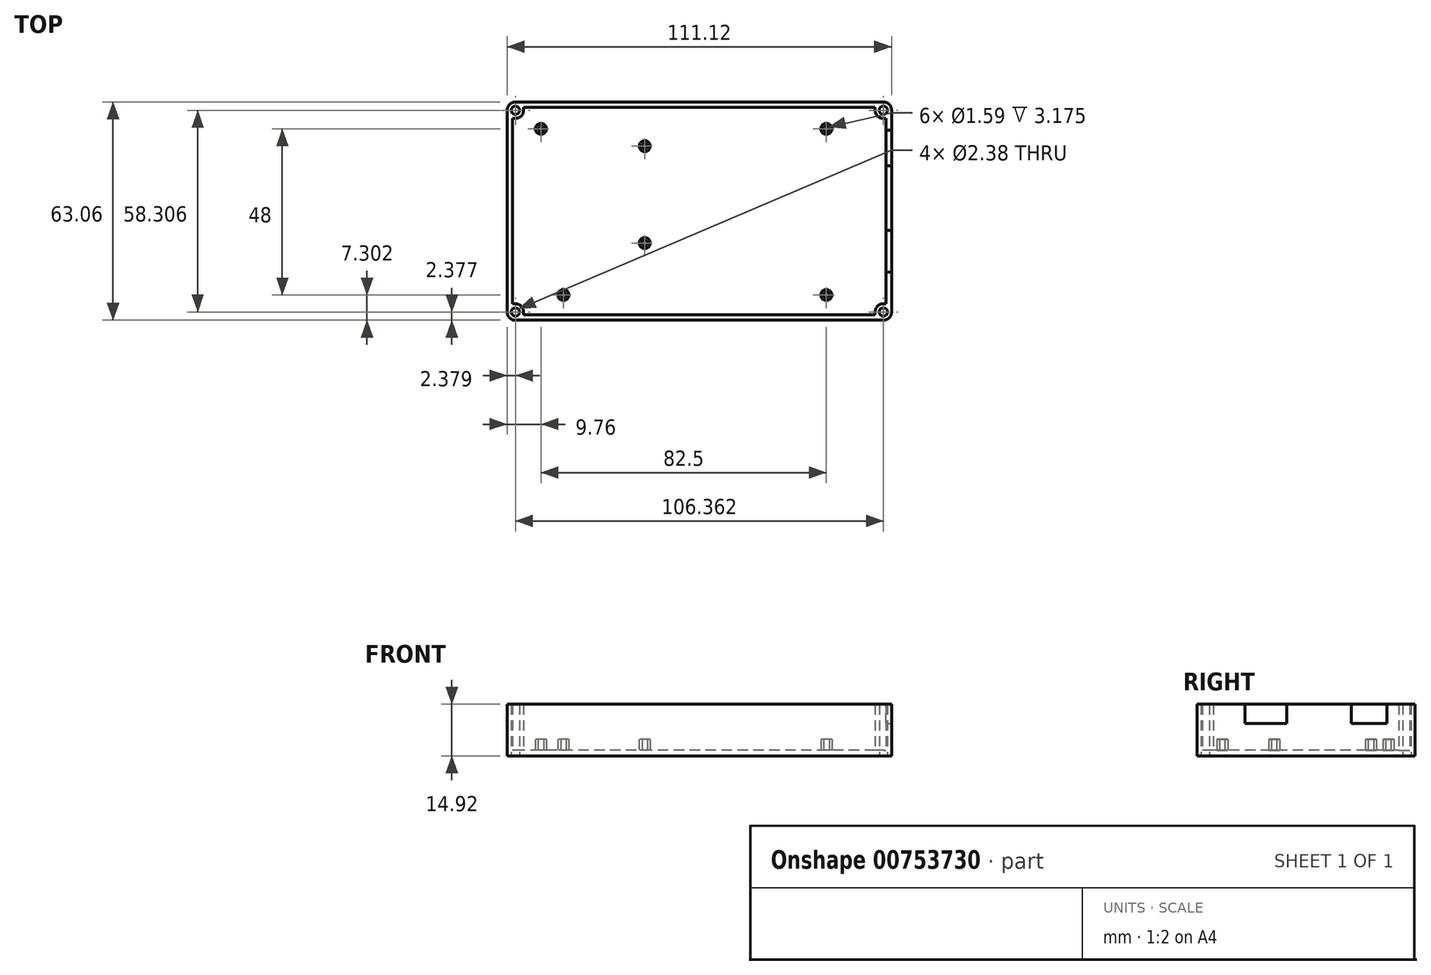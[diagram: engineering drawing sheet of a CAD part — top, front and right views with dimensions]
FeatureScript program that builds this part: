
annotation { "Feature Type Name" : "Feature", "Feature Type Description" : "" }
export const myFeature = defineFeature(function(context is Context, id is Id, definition is map)
    precondition{}
    {
        {
            var Q0;
            Q0=qCreatedBy(makeId("Top.planeOp"),FACE);
            var sketch = newSketch(context, id + "F0", { "sketchPlane" : qUnion([Q0])});
            skLineSegment(sketch, "E0.bottom", {"start": v(50.8, 26.77) * mm, "end": v(-50.8, 26.77) * mm});
            skLineSegment(sketch, "E0.top", {"start": v(50.8, -26.77) * mm, "end": v(-50.8, -26.77) * mm});
            skLineSegment(sketch, "E0.left", {"start": v(50.8, 26.77) * mm, "end": v(50.8, -26.77) * mm});
            skLineSegment(sketch, "E0.right", {"start": v(-50.8, 26.77) * mm, "end": v(-50.8, -26.77) * mm});
            skPoint(sketch, "E0.middle", {"position": v(0, 0) * mm});
            skSolve(sketch);
        }
        {
            var Q0;
            Q0=qCreatedBy(makeId("Top.planeOp"),FACE);
            var sketch = newSketch(context, id + "F1", { "sketchPlane" : qUnion([Q0])});
            skLineSegment(sketch, "E1.bottom", {"start": v(55.56, 31.53) * mm, "end": v(-55.56, 31.53) * mm});
            skLineSegment(sketch, "E1.top", {"start": v(55.56, -31.53) * mm, "end": v(-55.56, -31.53) * mm});
            skLineSegment(sketch, "E1.left", {"start": v(55.56, 31.53) * mm, "end": v(55.56, -31.53) * mm});
            skLineSegment(sketch, "E1.right", {"start": v(-55.56, 31.53) * mm, "end": v(-55.56, -31.53) * mm});
            skPoint(sketch, "E1.middle", {"position": v(0, 0) * mm});
            skLineSegment(sketch, "E2.bottom", {"start": v(53.97, 29.95) * mm, "end": v(-53.98, 29.95) * mm, "construction": true});
            skLineSegment(sketch, "E2.top", {"start": v(53.98, -29.95) * mm, "end": v(-53.97, -29.95) * mm, "construction": true});
            skLineSegment(sketch, "E2.left", {"start": v(53.97, 29.95) * mm, "end": v(53.98, -29.95) * mm, "construction": true});
            skLineSegment(sketch, "E2.right", {"start": v(-53.98, 29.95) * mm, "end": v(-53.97, -29.95) * mm, "construction": true});
            skSolve(sketch);
        }
        {
            var Q0;
            Q0=makeQuery(id+"F1.imprint","IMPRINT",FACE,{"disambiguationData":[TD([[makeQuery(id+"F1.imprint","IMPRINT",EDGE,{"derivedFrom":sQuery(id+"F1.wireOp",EDGE,"E1.bottom")}),1.0]])]});
            extrude(context, id + "F2", {"entities" : qUnion([Q0]), "depth" : 1.59 * mm, "offsetDistance" : 25.4 * mm});
        }
        {
            var Q0;
            Q0=makeQuery(id+"F2.opExtrude","CAP_FACE",FACE,{"disambiguationData":[OSD([sQuery(id+"F1.wireOp",EDGE,"E1.bottom"),sQuery(id+"F1.wireOp",EDGE,"E1.top"),sQuery(id+"F1.wireOp",EDGE,"E1.left"),sQuery(id+"F1.wireOp",EDGE,"E1.right")])],"isStart":false});
            var sketch = newSketch(context, id + "F3", { "sketchPlane" : qUnion([Q0])});
            skLineSegment(sketch, "E3.bottom", {"start": v(55.56, 31.53) * mm, "end": v(-55.56, 31.53) * mm});
            skLineSegment(sketch, "E3.top", {"start": v(55.56, -31.53) * mm, "end": v(-55.56, -31.53) * mm});
            skLineSegment(sketch, "E3.left", {"start": v(55.56, 31.53) * mm, "end": v(55.56, -31.53) * mm});
            skLineSegment(sketch, "E3.right", {"start": v(-55.56, 31.53) * mm, "end": v(-55.56, -31.53) * mm});
            skPoint(sketch, "E3.middle", {"position": v(0, 0) * mm});
            skLineSegment(sketch, "E4.left", {"start": v(53.97, 26.77) * mm, "end": v(53.97, -26.77) * mm});
            skLineSegment(sketch, "E4.right", {"start": v(-53.97, 26.77) * mm, "end": v(-53.97, -26.77) * mm});
            skArc(sketch, "E5", {"start": v(-53.18, 26.77) * mm, "mid": v(-51.5, 27.47) * mm, "end": v(-50.8, 29.15) * mm});
            skCircle(sketch, "E6", {"center": v(-53.18, 29.15) * mm, "radius": 1.2 * mm});
            skLineSegment(sketch, "E7", {"start": v(-50.8, 29.15) * mm, "end": v(-50.8, 29.95) * mm});
            skLineSegment(sketch, "E8", {"start": v(-53.18, 26.77) * mm, "end": v(-53.97, 26.77) * mm});
            skLineSegment(sketch, "E9", {"start": v(-55.56, 31.53) * mm, "end": v(-51.5, 27.47) * mm, "construction": true});
            skPoint(sketch, "E10", {"position": v(-53.53, 29.5) * mm});
            skPoint(sketch, "E11.orphan", {"position": v(-53.97, 37.1) * mm});
            skCircle(sketch, "E12.MirrorC", {"center": v(-53.18, -29.15) * mm, "radius": 1.2 * mm});
            skLineSegment(sketch, "E13.MirrorCS", {"start": v(-53.18, -26.77) * mm, "end": v(-53.97, -26.77) * mm});
            skArc(sketch, "E14.MirrorCS", {"start": v(-53.18, -26.77) * mm, "mid": v(-51.5, -27.47) * mm, "end": v(-50.8, -29.15) * mm});
            skLineSegment(sketch, "E15.MirrorCS", {"start": v(-50.8, -29.15) * mm, "end": v(-50.8, -29.95) * mm});
            skCircle(sketch, "E16.MirrorC", {"center": v(53.18, 29.15) * mm, "radius": 1.2 * mm});
            skLineSegment(sketch, "E17.MirrorCS", {"start": v(50.8, 29.15) * mm, "end": v(50.8, 29.95) * mm});
            skArc(sketch, "E18.MirrorCS", {"start": v(53.18, 26.77) * mm, "mid": v(51.5, 27.47) * mm, "end": v(50.8, 29.15) * mm});
            skLineSegment(sketch, "E19.MirrorCS", {"start": v(53.18, 26.77) * mm, "end": v(53.97, 26.77) * mm});
            skCircle(sketch, "E20.MirrorC", {"center": v(53.18, -29.15) * mm, "radius": 1.2 * mm});
            skLineSegment(sketch, "E21.MirrorCS", {"start": v(53.18, -26.77) * mm, "end": v(53.97, -26.77) * mm});
            skArc(sketch, "E22.MirrorCS", {"start": v(53.18, -26.77) * mm, "mid": v(51.5, -27.47) * mm, "end": v(50.8, -29.15) * mm});
            skLineSegment(sketch, "E23.MirrorCS", {"start": v(50.8, -29.15) * mm, "end": v(50.8, -29.95) * mm});
            skPoint(sketch, "E24.orphan", {"position": v(-53.97, -36.92) * mm});
            skLineSegment(sketch, "E25.trimOffspring", {"start": v(50.8, -29.95) * mm, "end": v(-50.8, -29.95) * mm});
            skPoint(sketch, "E26.orphan", {"position": v(53.97, -37.1) * mm});
            skLineSegment(sketch, "E27.trimOffspring", {"start": v(50.8, 29.95) * mm, "end": v(-50.8, 29.95) * mm});
            skPoint(sketch, "E28.orphan", {"position": v(53.97, 36.92) * mm});
            skSolve(sketch);
        }
        {
            var Q0;
            Q0=qSketchRegion(id+"F3",true);
            extrude(context, id + "F4", {"entities" : qUnion([Q0]), "operationType" : NewBodyOperationType.ADD, "depth" : 13.33 * mm, "offsetDistance" : 25.4 * mm});
        }
        {
            var Q0;
            Q0=makeQuery(id+"F4.boolean.opBoolean","MERGE",EDGE,{"derivedFrom":[makeQuery(id+"F2.opExtrude","SWEPT_EDGE",EDGE,{"disambiguationData":[OSD([sQuery(id+"F1.wireOp",EDGE,"E1.top"),sQuery(id+"F1.wireOp",EDGE,"E1.left")])]}),makeQuery(id+"F4.opExtrude","SWEPT_EDGE",EDGE,{"disambiguationData":[OSD([sQuery(id+"F3.wireOp",EDGE,"E3.top"),sQuery(id+"F3.wireOp",EDGE,"E3.left")])]})]});
            var Q1;
            Q1=makeQuery(id+"F4.boolean.opBoolean","MERGE",EDGE,{"derivedFrom":[makeQuery(id+"F2.opExtrude","SWEPT_EDGE",EDGE,{"disambiguationData":[OSD([sQuery(id+"F1.wireOp",EDGE,"E1.bottom"),sQuery(id+"F1.wireOp",EDGE,"E1.left")])]}),makeQuery(id+"F4.opExtrude","SWEPT_EDGE",EDGE,{"disambiguationData":[OSD([sQuery(id+"F3.wireOp",EDGE,"E3.bottom"),sQuery(id+"F3.wireOp",EDGE,"E3.left")])]})]});
            var Q2;
            Q2=makeQuery(id+"F4.boolean.opBoolean","MERGE",EDGE,{"derivedFrom":[makeQuery(id+"F2.opExtrude","SWEPT_EDGE",EDGE,{"disambiguationData":[OSD([sQuery(id+"F1.wireOp",EDGE,"E1.top"),sQuery(id+"F1.wireOp",EDGE,"E1.right")])]}),makeQuery(id+"F4.opExtrude","SWEPT_EDGE",EDGE,{"disambiguationData":[OSD([sQuery(id+"F3.wireOp",EDGE,"E3.top"),sQuery(id+"F3.wireOp",EDGE,"E3.right")])]})]});
            var Q3;
            Q3=makeQuery(id+"F4.boolean.opBoolean","MERGE",EDGE,{"derivedFrom":[makeQuery(id+"F2.opExtrude","SWEPT_EDGE",EDGE,{"disambiguationData":[OSD([sQuery(id+"F1.wireOp",EDGE,"E1.bottom"),sQuery(id+"F1.wireOp",EDGE,"E1.right")])]}),makeQuery(id+"F4.opExtrude","SWEPT_EDGE",EDGE,{"disambiguationData":[OSD([sQuery(id+"F3.wireOp",EDGE,"E3.bottom"),sQuery(id+"F3.wireOp",EDGE,"E3.right")])]})]});
            fillet(context, id + "F5", {"entities" : qUnion([Q0, Q1, Q2, Q3]), "radius" : 2.38 * mm, "tangentPropagation" : true, "allowEdgeOverflow" : false});
        }
        {
            var Q0;
            Q0=makeQuery(id+"F4.boolean.opBoolean","MERGE",FACE,{"derivedFrom":[makeQuery(id+"F2.opExtrude","SWEPT_FACE",FACE,{"disambiguationData":[OSD([sQuery(id+"F1.wireOp",EDGE,"E1.left")])]}),makeQuery(id+"F4.opExtrude","SWEPT_FACE",FACE,{"disambiguationData":[OSD([sQuery(id+"F3.wireOp",EDGE,"E3.left")])]})]});
            var sketch = newSketch(context, id + "F6", { "sketchPlane" : qUnion([Q0])});
            skLineSegment(sketch, "E29.bottom", {"start": v(-17.59, 14.92) * mm, "end": v(-5.52, 14.92) * mm});
            skLineSegment(sketch, "E29.top", {"start": v(-17.59, 9.4) * mm, "end": v(-5.52, 9.4) * mm});
            skLineSegment(sketch, "E29.left", {"start": v(-17.59, 14.92) * mm, "end": v(-17.59, 9.4) * mm});
            skLineSegment(sketch, "E29.right", {"start": v(-5.52, 14.92) * mm, "end": v(-5.52, 9.4) * mm});
            skLineSegment(sketch, "E30.bottom", {"start": v(13.14, 14.92) * mm, "end": v(23.43, 14.92) * mm});
            skLineSegment(sketch, "E30.top", {"start": v(13.14, 9.4) * mm, "end": v(23.43, 9.4) * mm});
            skLineSegment(sketch, "E30.left", {"start": v(13.14, 14.92) * mm, "end": v(13.14, 9.4) * mm});
            skLineSegment(sketch, "E30.right", {"start": v(23.43, 14.92) * mm, "end": v(23.43, 9.4) * mm});
            skPoint(sketch, "E31", {"position": v(-11.56, 9.4) * mm});
            skPoint(sketch, "E32", {"position": v(18.29, 9.4) * mm});
            skSolve(sketch);
        }
        {
            var Q0;
            Q0=qSketchRegion(id+"F6",true);
            extrude(context, id + "F7", {"entities" : qUnion([Q0]), "operationType" : NewBodyOperationType.REMOVE, "endBound" : BoundingType.UP_TO_NEXT, "oppositeDirection" : true, "depth" : 25.4 * mm, "offsetDistance" : 25.4 * mm});
        }
        {
            var Q0;
            Q0=makeQuery(id+"F4.boolean.opBoolean","SPLIT",FACE,{"disambiguationData":[TD([makeQuery(id+"F4.opExtrude","SWEPT_FACE",FACE,{"disambiguationData":[OSD([sQuery(id+"F3.wireOp",EDGE,"E4.left")])]})])],"derivedFrom":makeQuery(id+"F2.opExtrude","CAP_FACE",FACE,{"disambiguationData":[OSD([sQuery(id+"F1.wireOp",EDGE,"E1.bottom"),sQuery(id+"F1.wireOp",EDGE,"E1.top"),sQuery(id+"F1.wireOp",EDGE,"E1.left"),sQuery(id+"F1.wireOp",EDGE,"E1.right")])],"isStart":false})});
            var sketch = newSketch(context, id + "F8", { "sketchPlane" : qUnion([Q0])});
            skCircle(sketch, "E33", {"center": v(-45.8, 23.77) * mm, "radius": 0.8 * mm});
            skCircle(sketch, "E34", {"center": v(-39.3, -24.23) * mm, "radius": 0.8 * mm});
            skCircle(sketch, "E35", {"center": v(-15.8, 18.77) * mm, "radius": 0.8 * mm});
            skCircle(sketch, "E36", {"center": v(-15.8, -9.23) * mm, "radius": 0.8 * mm});
            skCircle(sketch, "E37", {"center": v(36.7, 23.77) * mm, "radius": 0.8 * mm});
            skCircle(sketch, "E38", {"center": v(36.7, -24.23) * mm, "radius": 0.8 * mm});
            skCircle(sketch, "E39", {"center": v(-45.8, 23.77) * mm, "radius": 1.59 * mm});
            skCircle(sketch, "E40", {"center": v(-39.3, -24.23) * mm, "radius": 1.59 * mm});
            skCircle(sketch, "E41", {"center": v(-15.8, 18.77) * mm, "radius": 1.59 * mm});
            skCircle(sketch, "E42", {"center": v(-15.8, -9.23) * mm, "radius": 1.59 * mm});
            skCircle(sketch, "E43", {"center": v(36.7, 23.77) * mm, "radius": 1.59 * mm});
            skCircle(sketch, "E44", {"center": v(36.7, -24.23) * mm, "radius": 1.59 * mm});
            skSolve(sketch);
        }
        {
            var Q0;
            Q0=qSketchRegion(id+"F8",true);
            extrude(context, id + "F9", {"entities" : qUnion([Q0]), "operationType" : NewBodyOperationType.ADD, "depth" : 3.17 * mm, "offsetDistance" : 25.4 * mm});
        }
        {
            var Q0;
            {var subQ0=sQuery(id+"F3.wireOp",EDGE,"E18.MirrorCS");var subQ1=sQuery(id+"F3.wireOp",EDGE,"E17.MirrorCS");var subQ2=sQuery(id+"F3.wireOp",EDGE,"E16.MirrorC");var subQ3=sQuery(id+"F3.wireOp",EDGE,"E15.MirrorCS");var subQ4=sQuery(id+"F3.wireOp",EDGE,"E14.MirrorCS");var subQ5=sQuery(id+"F3.wireOp",EDGE,"E13.MirrorCS");var subQ6=sQuery(id+"F3.wireOp",EDGE,"E12.MirrorC");var subQ7=sQuery(id+"F3.wireOp",EDGE,"E8");var subQ8=sQuery(id+"F3.wireOp",EDGE,"E7");var subQ9=sQuery(id+"F3.wireOp",EDGE,"E6");var subQ10=sQuery(id+"F3.wireOp",EDGE,"E5");var subQ11=sQuery(id+"F3.wireOp",EDGE,"E3.top");var subQ12=sQuery(id+"F3.wireOp",EDGE,"E3.left");var subQ13=sQuery(id+"F3.wireOp",EDGE,"E3.bottom");var subQ15=sQuery(id+"F1.wireOp",EDGE,"E1.bottom");var subQ17=sQuery(id+"F3.wireOp",EDGE,"E22.MirrorCS");var subQ19=sQuery(id+"F3.wireOp",EDGE,"E25.trimOffspring");var subQ20=sQuery(id+"F3.wireOp",EDGE,"E3.right");var subQ21=sQuery(id+"F3.wireOp",EDGE,"E19.MirrorCS");var subQ22=sQuery(id+"F3.wireOp",EDGE,"E23.MirrorCS");var subQ23=sQuery(id+"F3.wireOp",EDGE,"E4.left");var subQ24=sQuery(id+"F3.wireOp",EDGE,"E4.right");var subQ25=sQuery(id+"F3.wireOp",EDGE,"E20.MirrorC");var subQ26=sQuery(id+"F3.wireOp",EDGE,"E21.MirrorCS");var subQ27=sQuery(id+"F3.wireOp",EDGE,"E27.trimOffspring");Q0=makeQuery(id+"F7.boolean.opBoolean","SPLIT",FACE,{"disambiguationData":[TD([makeQuery(id+"F2.opExtrude","SWEPT_FACE",FACE,{"disambiguationData":[OSD([subQ15])]})])],"derivedFrom":makeQuery(id+"F4.opExtrude","CAP_FACE",FACE,{"disambiguationData":[OSD([subQ13,subQ11,subQ12,subQ20,subQ23,subQ24,subQ10,subQ9,subQ8,subQ7,subQ6,subQ5,subQ4,subQ3,subQ2,subQ1,subQ0,subQ21,subQ25,subQ26,subQ17,subQ22,subQ19,subQ27])],"isStart":false})});}
            var sketch = newSketch(context, id + "F10", { "sketchPlane" : qUnion([Q0])});
            skCircle(sketch, "E45.0", {"center": v(-53.18, 29.15) * mm, "radius": 1.2 * mm});
            skCircle(sketch, "E46.0", {"center": v(-53.18, -29.15) * mm, "radius": 1.2 * mm});
            skCircle(sketch, "E47.0", {"center": v(53.18, -29.15) * mm, "radius": 1.2 * mm});
            skCircle(sketch, "E48.0", {"center": v(53.18, 29.15) * mm, "radius": 1.2 * mm});
            skSolve(sketch);
        }
        {
            var Q0;
            Q0=qSketchRegion(id+"F10",true);
            extrude(context, id + "F11", {"entities" : qUnion([Q0]), "operationType" : NewBodyOperationType.REMOVE, "endBound" : BoundingType.THROUGH_ALL, "oppositeDirection" : true, "depth" : 25.4 * mm, "offsetDistance" : 25.4 * mm});
        }
    });
